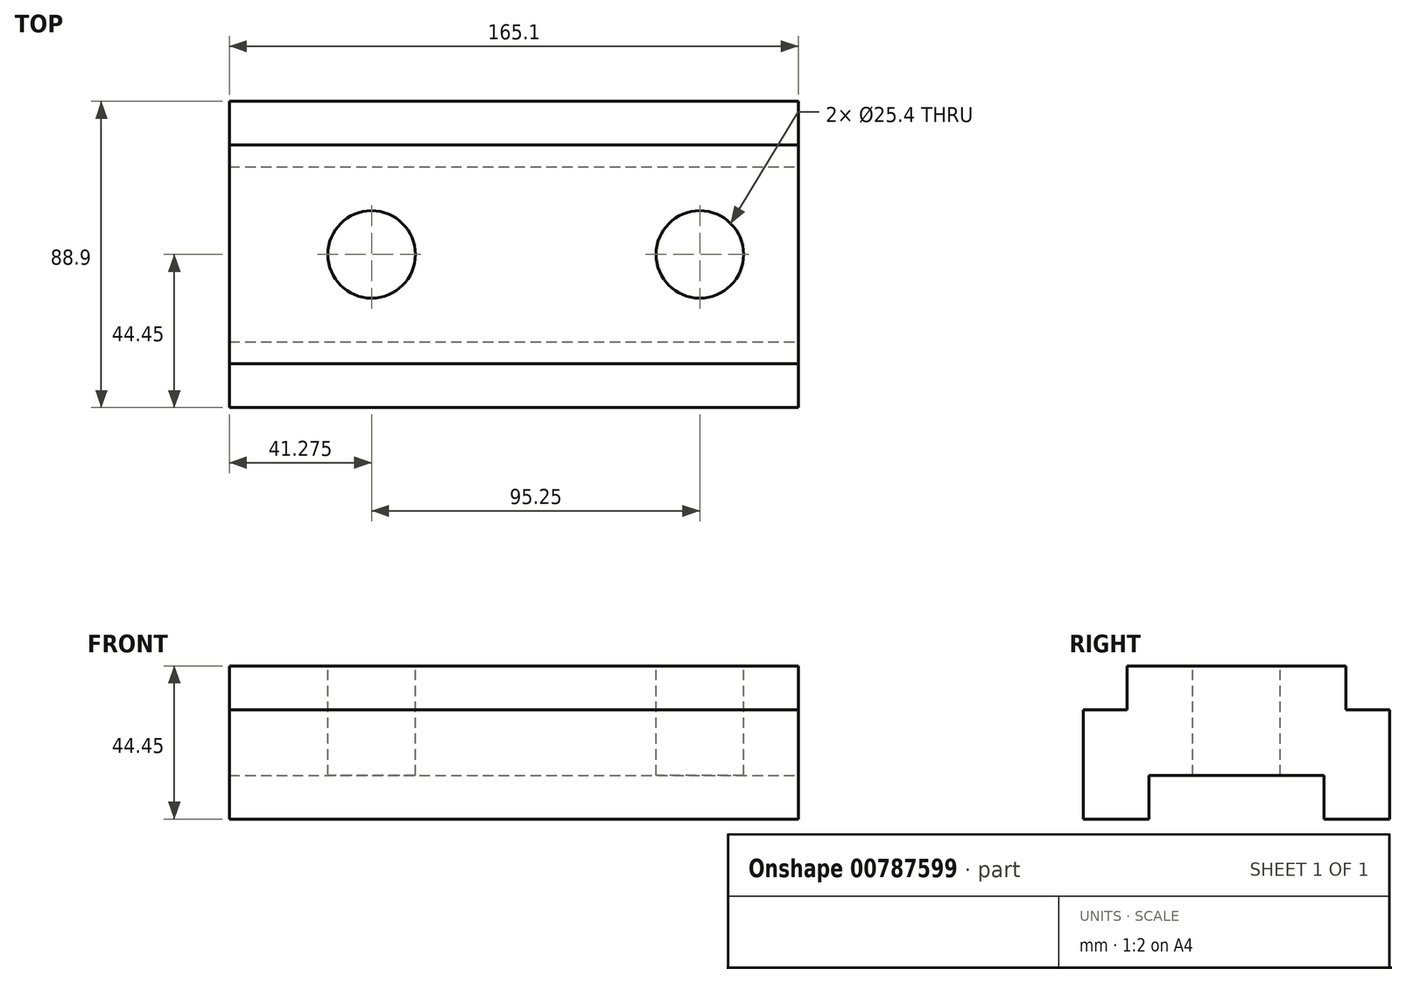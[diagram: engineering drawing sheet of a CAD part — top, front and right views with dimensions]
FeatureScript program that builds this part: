
annotation { "Feature Type Name" : "Feature", "Feature Type Description" : "" }
export const myFeature = defineFeature(function(context is Context, id is Id, definition is map)
    precondition{}
    {
        {
            var Q0;
            Q0=qCreatedBy(makeId("Front.planeOp"),FACE);
            var sketch = newSketch(context, id + "F0", { "sketchPlane" : qUnion([Q0])});
            skLineSegment(sketch, "E0", {"start": v(0, 0) * mm, "end": v(165.1, 0) * mm});
            skLineSegment(sketch, "E1", {"start": v(0, 0) * mm, "end": v(0, 44.45) * mm});
            skLineSegment(sketch, "E2", {"start": v(0, 44.45) * mm, "end": v(165.1, 44.45) * mm});
            skLineSegment(sketch, "E3", {"start": v(165.1, 44.45) * mm, "end": v(165.1, 0) * mm});
            skSolve(sketch);
        }
        {
            var Q0;
            Q0 = qSketchRegion(id + "F0", true);
            extrude(context, id + "F1", {"entities" : qUnion([Q0]), "depth" : 88.9 * mm, "offsetDistance" : 25.4 * mm});
        }
        {
            var Q0;
            Q0=makeQuery(id+"F1.opExtrude","SWEPT_FACE",FACE,{"disambiguationData":[OSD([sQuery(id+"F0.wireOp",EDGE,"E3")])]});
            var sketch = newSketch(context, id + "F2", { "sketchPlane" : qUnion([Q0])});
            skLineSegment(sketch, "E4", {"start": v(-88.9, 0) * mm, "end": v(-69.85, 0) * mm});
            skLineSegment(sketch, "E5", {"start": v(-69.85, 0) * mm, "end": v(-69.85, 12.7) * mm});
            skLineSegment(sketch, "E6", {"start": v(0, 0) * mm, "end": v(-19.05, 0) * mm});
            skLineSegment(sketch, "E7", {"start": v(-19.05, 0) * mm, "end": v(-19.05, 12.7) * mm});
            skLineSegment(sketch, "E8", {"start": v(-19.05, 12.7) * mm, "end": v(-69.85, 12.7) * mm});
            skLineSegment(sketch, "E9", {"start": v(-88.9, 44.45) * mm, "end": v(-88.9, 31.75) * mm});
            skLineSegment(sketch, "E10", {"start": v(-88.9, 44.45) * mm, "end": v(-76.2, 44.45) * mm});
            skLineSegment(sketch, "E11", {"start": v(-76.2, 44.45) * mm, "end": v(-76.2, 31.75) * mm});
            skLineSegment(sketch, "E12", {"start": v(-76.2, 31.75) * mm, "end": v(-88.9, 31.75) * mm});
            skLineSegment(sketch, "E13", {"start": v(0, 44.45) * mm, "end": v(-12.7, 44.45) * mm});
            skLineSegment(sketch, "E14", {"start": v(0, 44.45) * mm, "end": v(0, 31.75) * mm});
            skLineSegment(sketch, "E15", {"start": v(-12.7, 44.45) * mm, "end": v(-12.7, 31.75) * mm});
            skLineSegment(sketch, "E16", {"start": v(-12.7, 31.75) * mm, "end": v(0, 31.75) * mm});
            skSolve(sketch);
        }
        {
            var Q0;
            Q0 = qSketchRegion(id + "F2", true);
            var Q1;
            {var subQ0=sQuery(id+"F2.wireOp",EDGE,"E5");Q1=makeQuery(id+"F2.imprint","IMPRINT",FACE,{"disambiguationData":[TD([[makeQuery(id+"F2.imprint","IMPRINT",EDGE,{"derivedFrom":subQ0}),-1.0]])]});}
            extrude(context, id + "F3", {"entities" : qUnion([Q0, Q1]), "operationType" : NewBodyOperationType.REMOVE, "oppositeDirection" : true, "depth" : 165.1 * mm, "offsetDistance" : 25.4 * mm});
        }
        {
            var Q0;
            Q0=makeQuery(id+"F1.opExtrude","SWEPT_FACE",FACE,{"disambiguationData":[OSD([sQuery(id+"F0.wireOp",EDGE,"E2")])]});
            var sketch = newSketch(context, id + "F4", { "sketchPlane" : qUnion([Q0])});
            skLineSegment(sketch, "E17", {"start": v(0, -44.45) * mm, "end": v(41.28, -44.45) * mm, "construction": true});
            skLineSegment(sketch, "E18", {"start": v(41.28, -44.45) * mm, "end": v(136.53, -44.45) * mm, "construction": true});
            skCircle(sketch, "E19", {"center": v(41.28, -44.45) * mm, "radius": 12.7 * mm, "construction": true});
            skCircle(sketch, "E20", {"center": v(136.53, -44.45) * mm, "radius": 12.7 * mm, "construction": true});
            skCircle(sketch, "E21", {"center": v(41.28, -44.45) * mm, "radius": 12.7 * mm});
            skCircle(sketch, "E22", {"center": v(136.53, -44.45) * mm, "radius": 12.7 * mm});
            skSolve(sketch);
        }
        {
            var Q0;
            Q0=makeQuery(id+"F4.imprint","IMPRINT",FACE,{"disambiguationData":[TD([[makeQuery(id+"F4.imprint","IMPRINT",EDGE,{"derivedFrom":sQuery(id+"F4.wireOp",EDGE,"E21")}),1.0]])]});
            var Q1;
            Q1=makeQuery(id+"F4.imprint","IMPRINT",FACE,{"disambiguationData":[TD([[makeQuery(id+"F4.imprint","IMPRINT",EDGE,{"derivedFrom":sQuery(id+"F4.wireOp",EDGE,"E22")}),1.0]])]});
            extrude(context, id + "F5", {"entities" : qUnion([Q0, Q1]), "operationType" : NewBodyOperationType.REMOVE, "oppositeDirection" : true, "depth" : 254 * mm, "offsetDistance" : 25.4 * mm});
        }
    });
